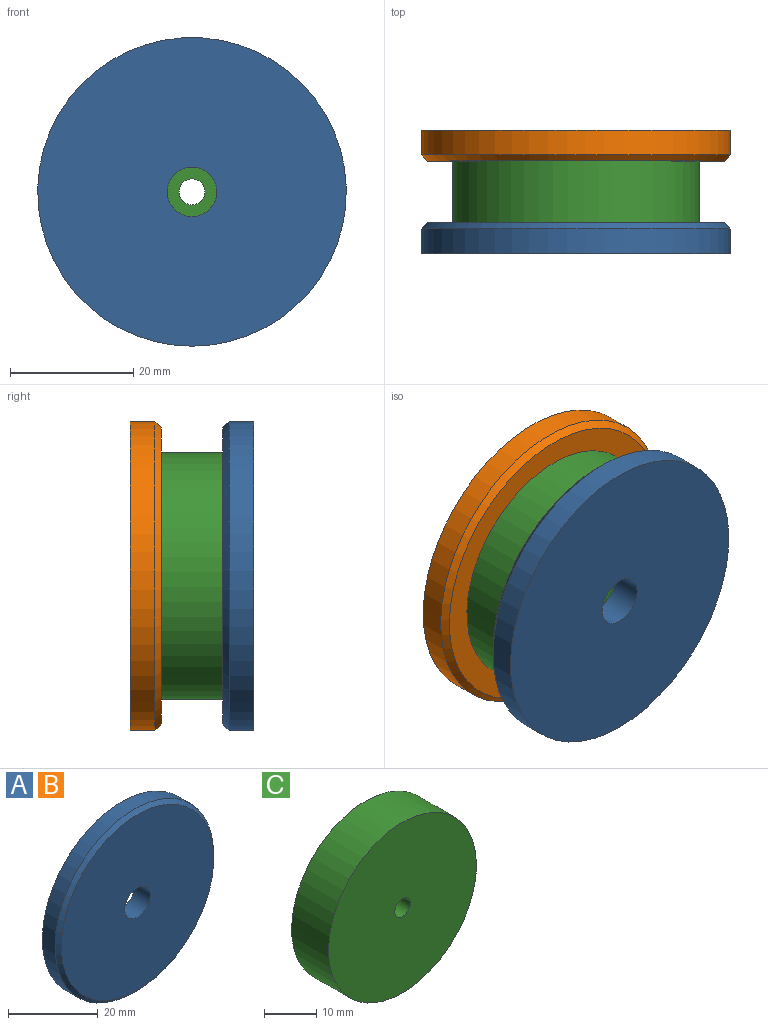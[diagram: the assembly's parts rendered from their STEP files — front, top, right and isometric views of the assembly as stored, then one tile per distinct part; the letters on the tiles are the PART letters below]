
ASSEMBLY  parts=3 mates=2
PART A: 5 faces, bbox 50x5x50 mm
  f0: cylinder r=4mm len=8mm, axis (0,1,0), area 125.7mm2, adj f2,f3
  f1: cylinder r=25mm len=50mm, axis (0,1,0), area 628.3mm2, adj f3,f4
  f2: plane 48x48mm, normal (0,-1,0), area 1759.3mm2, adj f0,f4
  f3: plane 50x50mm, normal (0,1,0), area 1913.2mm2, adj f0,f1
  f4: cone r=24mm half-angle=45deg, axis (0,1,0), area 217.7mm2, adj f1,f2
PART B: same geometry as A
PART C: 4 faces, bbox 40x10x40 mm
  f0: cylinder r=2.1mm len=10mm, axis (0,1,0), area 131.9mm2, adj f2,f3
  f1: cylinder r=20mm len=40mm, axis (0,1,0), area 1256.6mm2, adj f2,f3
  f2: plane 40x40mm, normal (0,-1,0), area 1242.8mm2, adj f0,f1
  f3: plane 40x40mm, normal (0,1,0), area 1242.8mm2, adj f0,f1
PLACE A rot(axis=(0,0,1),180deg) t=(0,-20,0)mm
PLACE B at identity
PLACE C t=(0,-5,0)mm
MATE fastened C.f1 <-> A.f0  axis (0,-1,0) through (0,-15,0)mm
MATE fastened B.f0 <-> C.f0  axis (0,-1,0) through (0,-5,0)mm
